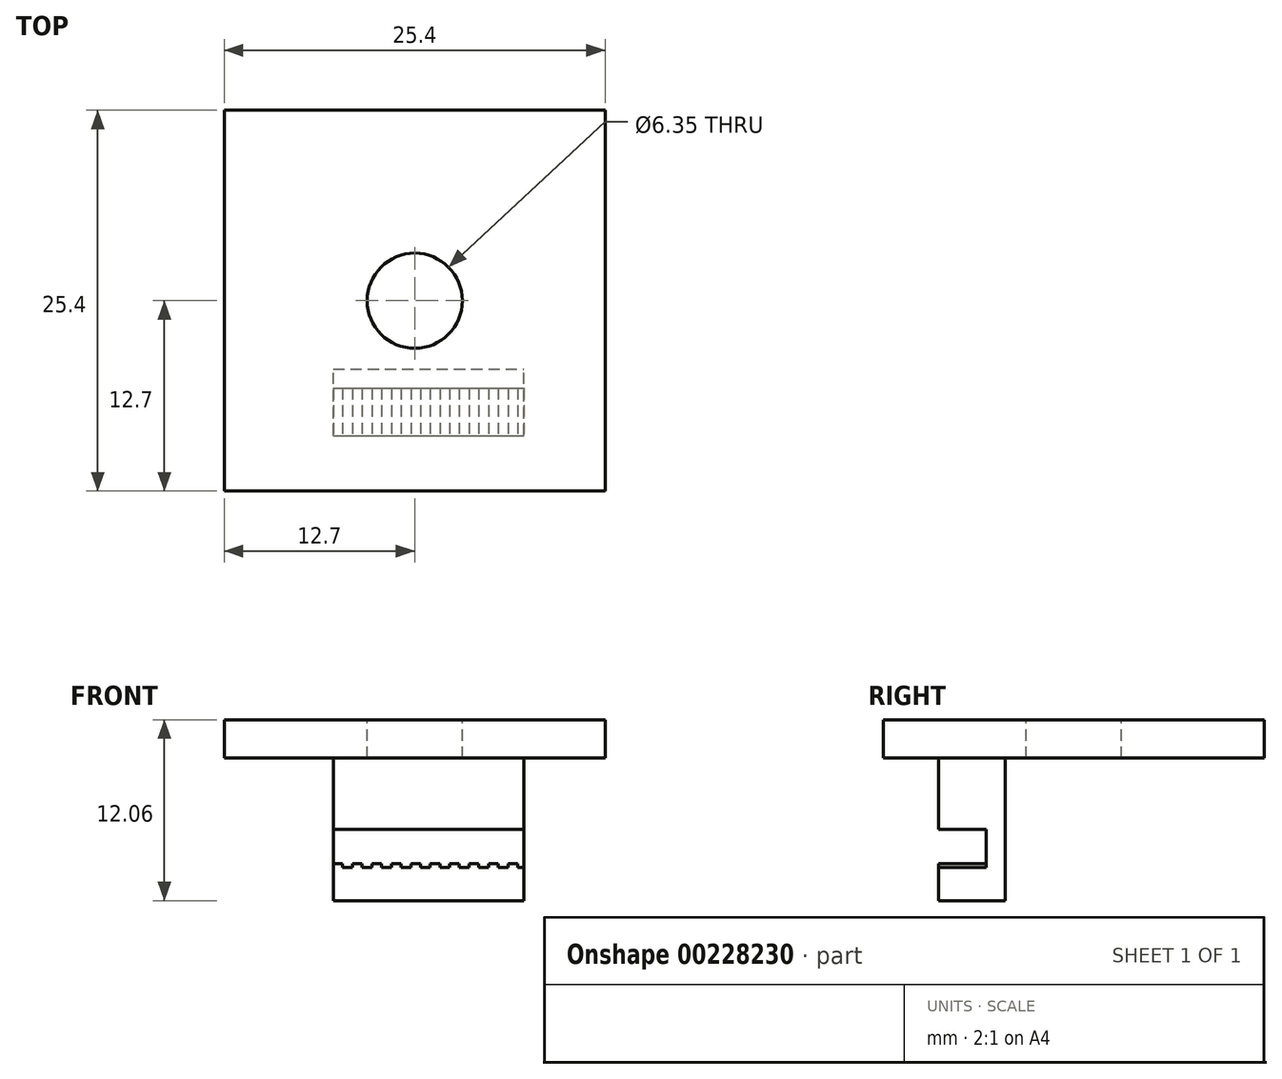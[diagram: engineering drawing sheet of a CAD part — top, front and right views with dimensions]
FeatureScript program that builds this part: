
annotation { "Feature Type Name" : "Feature", "Feature Type Description" : "" }
export const myFeature = defineFeature(function(context is Context, id is Id, definition is map)
    precondition{}
    {
        {
            var Q0;
            Q0=qCreatedBy(makeId("Right.planeOp"),FACE);
            var sketch = newSketch(context, id + "F0", { "sketchPlane" : qUnion([Q0])});
            skLineSegment(sketch, "E0.bottom", {"start": v(12.7, -1.27) * mm, "end": v(-12.7, -1.27) * mm});
            skLineSegment(sketch, "E0.top", {"start": v(12.7, 1.27) * mm, "end": v(-12.7, 1.27) * mm});
            skLineSegment(sketch, "E0.left", {"start": v(12.7, -1.27) * mm, "end": v(12.7, 1.27) * mm});
            skLineSegment(sketch, "E0.right", {"start": v(-12.7, -1.27) * mm, "end": v(-12.7, 1.27) * mm});
            skPoint(sketch, "E0.middle", {"position": v(0, 0) * mm});
            skSolve(sketch);
        }
        {
            var Q0;
            Q0=makeQuery(id+"F0.imprint","IMPRINT",FACE,{"disambiguationData":[TD([[makeQuery(id+"F0.imprint","IMPRINT",EDGE,{"derivedFrom":sQuery(id+"F0.wireOp",EDGE,"E0.bottom")}),-1.0]])]});
            extrude(context, id + "F1", {"entities" : qUnion([Q0]), "depth" : 25.4 * mm});
        }
        {
            var Q0;
            Q0=makeQuery(id+"F1.opExtrude","SWEPT_FACE",FACE,{"disambiguationData":[OSD([sQuery(id+"F0.wireOp",EDGE,"E0.top")])]});
            var sketch = newSketch(context, id + "F2", { "sketchPlane" : qUnion([Q0])});
            skCircle(sketch, "E1", {"center": v(12.7, 0) * mm, "radius": 3.18 * mm});
            skSolve(sketch);
        }
        {
            var Q0;
            Q0=makeQuery(id+"F2.imprint","IMPRINT",FACE,{"disambiguationData":[TD([[makeQuery(id+"F2.imprint","IMPRINT",EDGE,{"derivedFrom":sQuery(id+"F2.wireOp",EDGE,"E1")}),1.0]])]});
            extrude(context, id + "F3", {"entities" : qUnion([Q0]), "operationType" : NewBodyOperationType.REMOVE, "oppositeDirection" : true, "depth" : 25.4 * mm});
        }
        {
            var Q0;
            Q0=makeQuery(id+"F1.opExtrude","SWEPT_FACE",FACE,{"disambiguationData":[OSD([sQuery(id+"F0.wireOp",EDGE,"E0.bottom")])]});
            var sketch = newSketch(context, id + "F4", { "sketchPlane" : qUnion([Q0])});
            skLineSegment(sketch, "E2.bottom", {"start": v(7.26, 9) * mm, "end": v(19.96, 9) * mm});
            skLineSegment(sketch, "E2.top", {"start": v(7.26, 4.56) * mm, "end": v(19.96, 4.56) * mm});
            skLineSegment(sketch, "E2.left", {"start": v(7.26, 9) * mm, "end": v(7.26, 4.56) * mm});
            skLineSegment(sketch, "E2.right", {"start": v(19.96, 9) * mm, "end": v(19.96, 4.56) * mm});
            skSolve(sketch);
        }
        {
            var Q0;
            Q0=makeQuery(id+"F4.imprint","IMPRINT",FACE,{"disambiguationData":[TD([[makeQuery(id+"F4.imprint","IMPRINT",EDGE,{"derivedFrom":sQuery(id+"F4.wireOp",EDGE,"E2.bottom")}),-1.0]])]});
            extrude(context, id + "F5", {"entities" : qUnion([Q0]), "operationType" : NewBodyOperationType.ADD, "depth" : 9.52 * mm});
        }
        {
            var Q0;
            Q0=makeQuery(id+"F5.opExtrude","SWEPT_FACE",FACE,{"disambiguationData":[OSD([sQuery(id+"F4.wireOp",EDGE,"E2.bottom")])]});
            var sketch = newSketch(context, id + "F6", { "sketchPlane" : qUnion([Q0])});
            skLineSegment(sketch, "E3.bottom", {"start": v(7.26, -8.57) * mm, "end": v(19.96, -8.57) * mm});
            skLineSegment(sketch, "E3.top", {"start": v(7.26, -6.03) * mm, "end": v(19.96, -6.03) * mm});
            skLineSegment(sketch, "E3.left", {"start": v(7.26, -8.57) * mm, "end": v(7.26, -6.03) * mm});
            skLineSegment(sketch, "E3.right", {"start": v(19.96, -8.57) * mm, "end": v(19.96, -6.03) * mm});
            skSolve(sketch);
        }
        {
            var Q0;
            Q0=makeQuery(id+"F6.imprint","IMPRINT",FACE,{"disambiguationData":[TD([[makeQuery(id+"F6.imprint","IMPRINT",EDGE,{"derivedFrom":sQuery(id+"F6.wireOp",EDGE,"E3.bottom")}),1.0]])]});
            extrude(context, id + "F7", {"entities" : qUnion([Q0]), "operationType" : NewBodyOperationType.REMOVE, "oppositeDirection" : true, "depth" : 3.17 * mm});
        }
        {
            var Q0;
            Q0=makeQuery(id+"F7.boolean.opBoolean","COPY",FACE,{"derivedFrom":makeQuery(id+"F7.opExtrude","SWEPT_FACE",FACE,{"disambiguationData":[OSD([sQuery(id+"F6.wireOp",EDGE,"E3.bottom")])]})});
            var sketch = newSketch(context, id + "F8", { "sketchPlane" : qUnion([Q0])});
            skLineSegment(sketch, "E4.bottom", {"start": v(7.26, -5.83) * mm, "end": v(7.9, -5.83) * mm});
            skLineSegment(sketch, "E4.top", {"start": v(7.26, -9) * mm, "end": v(7.9, -9) * mm});
            skLineSegment(sketch, "E4.left", {"start": v(7.26, -5.83) * mm, "end": v(7.26, -9) * mm});
            skLineSegment(sketch, "E4.right", {"start": v(7.9, -5.83) * mm, "end": v(7.9, -9) * mm});
            skLineSegment(sketch, "E5.1.0.0", {"start": v(9.2, -5.83) * mm, "end": v(9.2, -9) * mm});
            skLineSegment(sketch, "E5.1.0.1", {"start": v(8.56, -5.83) * mm, "end": v(9.2, -5.83) * mm});
            skLineSegment(sketch, "E5.1.0.2", {"start": v(8.56, -5.83) * mm, "end": v(8.56, -9) * mm});
            skLineSegment(sketch, "E5.2.0.0", {"start": v(10.49, -5.83) * mm, "end": v(10.49, -9) * mm});
            skLineSegment(sketch, "E5.2.0.1", {"start": v(9.85, -5.83) * mm, "end": v(10.49, -5.83) * mm});
            skLineSegment(sketch, "E5.2.0.2", {"start": v(9.85, -5.83) * mm, "end": v(9.85, -9) * mm});
            skLineSegment(sketch, "E5.3.0.0", {"start": v(11.78, -5.83) * mm, "end": v(11.78, -9) * mm});
            skLineSegment(sketch, "E5.3.0.1", {"start": v(11.15, -5.83) * mm, "end": v(11.78, -5.83) * mm});
            skLineSegment(sketch, "E5.3.0.2", {"start": v(11.15, -5.83) * mm, "end": v(11.15, -9) * mm});
            skLineSegment(sketch, "E5.4.0.0", {"start": v(13.08, -5.83) * mm, "end": v(13.08, -9) * mm});
            skLineSegment(sketch, "E5.4.0.1", {"start": v(12.44, -5.83) * mm, "end": v(13.08, -5.83) * mm});
            skLineSegment(sketch, "E5.4.0.2", {"start": v(12.44, -5.83) * mm, "end": v(12.44, -9) * mm});
            skLineSegment(sketch, "E5.5.0.0", {"start": v(14.37, -5.83) * mm, "end": v(14.37, -9) * mm});
            skLineSegment(sketch, "E5.5.0.1", {"start": v(13.74, -5.83) * mm, "end": v(14.37, -5.83) * mm});
            skLineSegment(sketch, "E5.5.0.2", {"start": v(13.74, -5.83) * mm, "end": v(13.74, -9) * mm});
            skLineSegment(sketch, "E5.6.0.0", {"start": v(15.67, -5.83) * mm, "end": v(15.67, -9) * mm});
            skLineSegment(sketch, "E5.6.0.1", {"start": v(15.03, -5.83) * mm, "end": v(15.67, -5.83) * mm});
            skLineSegment(sketch, "E5.6.0.2", {"start": v(15.03, -5.83) * mm, "end": v(15.03, -9) * mm});
            skLineSegment(sketch, "E5.7.0.0", {"start": v(16.96, -5.83) * mm, "end": v(16.96, -9) * mm});
            skLineSegment(sketch, "E5.7.0.1", {"start": v(16.33, -5.83) * mm, "end": v(16.96, -5.83) * mm});
            skLineSegment(sketch, "E5.7.0.2", {"start": v(16.33, -5.83) * mm, "end": v(16.33, -9) * mm});
            skLineSegment(sketch, "E5.8.0.0", {"start": v(18.26, -5.83) * mm, "end": v(18.26, -9) * mm});
            skLineSegment(sketch, "E5.8.0.1", {"start": v(17.62, -5.83) * mm, "end": v(18.26, -5.83) * mm});
            skLineSegment(sketch, "E5.8.0.2", {"start": v(17.62, -5.83) * mm, "end": v(17.62, -9) * mm});
            skLineSegment(sketch, "E5.9.0.0", {"start": v(19.55, -5.83) * mm, "end": v(19.55, -9) * mm});
            skLineSegment(sketch, "E5.9.0.1", {"start": v(18.92, -5.83) * mm, "end": v(19.55, -5.83) * mm});
            skLineSegment(sketch, "E5.9.0.2", {"start": v(18.92, -5.83) * mm, "end": v(18.92, -9) * mm});
            skLineSegment(sketch, "E5.direction1", {"start": v(7.9, -9) * mm, "end": v(9.2, -9) * mm, "construction": true});
            skSolve(sketch);
        }
        {
            var Q0;
            {var subQ0=sQuery(id+"F8.wireOp",EDGE,"E5.1.0.0");Q0=makeQuery(id+"F8.imprint","IMPRINT",FACE,{"disambiguationData":[TD([[makeQuery(id+"F8.imprint","IMPRINT",EDGE,{"derivedFrom":subQ0}),-1.0]])]});}
            var Q1;
            Q1=makeQuery(id+"F8.imprint","IMPRINT",FACE,{"disambiguationData":[TD([[makeQuery(id+"F8.imprint","IMPRINT",EDGE,{"derivedFrom":sQuery(id+"F8.wireOp",EDGE,"E4.bottom")}),-1.0]])]});
            var Q2;
            {var subQ0=sQuery(id+"F8.wireOp",EDGE,"E5.2.0.0");Q2=makeQuery(id+"F8.imprint","IMPRINT",FACE,{"disambiguationData":[TD([[makeQuery(id+"F8.imprint","IMPRINT",EDGE,{"derivedFrom":subQ0}),-1.0]])]});}
            var Q3;
            {var subQ0=sQuery(id+"F8.wireOp",EDGE,"E5.3.0.0");Q3=makeQuery(id+"F8.imprint","IMPRINT",FACE,{"disambiguationData":[TD([[makeQuery(id+"F8.imprint","IMPRINT",EDGE,{"derivedFrom":subQ0}),-1.0]])]});}
            var Q4;
            {var subQ0=sQuery(id+"F8.wireOp",EDGE,"E5.4.0.0");Q4=makeQuery(id+"F8.imprint","IMPRINT",FACE,{"disambiguationData":[TD([[makeQuery(id+"F8.imprint","IMPRINT",EDGE,{"derivedFrom":subQ0}),-1.0]])]});}
            var Q5;
            {var subQ0=sQuery(id+"F8.wireOp",EDGE,"E5.5.0.0");Q5=makeQuery(id+"F8.imprint","IMPRINT",FACE,{"disambiguationData":[TD([[makeQuery(id+"F8.imprint","IMPRINT",EDGE,{"derivedFrom":subQ0}),-1.0]])]});}
            var Q6;
            {var subQ0=sQuery(id+"F8.wireOp",EDGE,"E5.6.0.0");Q6=makeQuery(id+"F8.imprint","IMPRINT",FACE,{"disambiguationData":[TD([[makeQuery(id+"F8.imprint","IMPRINT",EDGE,{"derivedFrom":subQ0}),-1.0]])]});}
            var Q7;
            {var subQ0=sQuery(id+"F8.wireOp",EDGE,"E5.7.0.0");Q7=makeQuery(id+"F8.imprint","IMPRINT",FACE,{"disambiguationData":[TD([[makeQuery(id+"F8.imprint","IMPRINT",EDGE,{"derivedFrom":subQ0}),-1.0]])]});}
            var Q8;
            {var subQ0=sQuery(id+"F8.wireOp",EDGE,"E5.8.0.0");Q8=makeQuery(id+"F8.imprint","IMPRINT",FACE,{"disambiguationData":[TD([[makeQuery(id+"F8.imprint","IMPRINT",EDGE,{"derivedFrom":subQ0}),-1.0]])]});}
            var Q9;
            {var subQ0=sQuery(id+"F8.wireOp",EDGE,"E5.9.0.0");Q9=makeQuery(id+"F8.imprint","IMPRINT",FACE,{"disambiguationData":[TD([[makeQuery(id+"F8.imprint","IMPRINT",EDGE,{"derivedFrom":subQ0}),-1.0]])]});}
            extrude(context, id + "F9", {"entities" : qUnion([Q0, Q1, Q2, Q3, Q4, Q5, Q6, Q7, Q8, Q9]), "operationType" : NewBodyOperationType.ADD, "depth" : 0.25 * mm});
        }
    });
